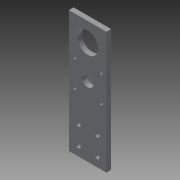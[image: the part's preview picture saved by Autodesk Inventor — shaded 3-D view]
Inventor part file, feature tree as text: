
AUTODESK INVENTOR PART (.ipt)
format: ipt  version: 2013 (Build 170138000, 138)  size: 223,744 bytes
history: native  units: in
note: dims shown in document units (in); Inventor stores cm internally (conversion verified against a paired STEP export)
features: extrude x12, sketch x12
ambient origin geometry x8: Origin, YZ Plane, XZ Plane, XY Plane, X Axis, Y Axis, Z Axis, Center Point
bodies: Solid1 (feature_tree)
feature tree (24):
  extrude  "Extrusion1"  Depth=6.688in
  extrude  "Extrusion2"  TaperAngle=90.0deg  [1 undecoded]
  extrude  "Extrusion3"  Depth=1.0in
  extrude  "Extrusion4"  Depth=2.0in
  extrude  "Extrusion5"  Depth=0.16in
  extrude  "Extrusion6"  Depth=0.16in
  extrude  "Extrusion7"  Depth=1.5in
  extrude  "Extrusion8"  TaperAngle=180.0deg  [1 undecoded]
  extrude  "Extrusion9"  TaperAngle=0.0deg  [1 undecoded]
  extrude  "Extrusion10"  Depth=0.25in
  extrude  "Extrusion11"  Depth=0.125in
  extrude  "Extrusion12"  Depth=1.75in
  sketch  "Sketch1"  dims[d0=2.0in d1=6.688in]
  sketch  "Sketch2"  dims[d2=1.0in d3=90.0deg]
  sketch  "Sketch3"  dims[d4=1.125in d5=1.0in]
  sketch  "Sketch4"  dims[d6=45.0deg d7=2.0in]
  sketch  "Sketch5"  dims[d9=0.16in d10=0.16in]
  sketch  "Sketch6"  dims[d11=0.16in d12=0.16in]
  sketch  "Sketch7"  dims[d13=2.0in d14=1.5in]
  sketch  "Sketch8"  dims[d15=0.5in d16=180.0deg]
  sketch  "Sketch9"  dims[d17=1.0in d18=0.0in]
  sketch  "Sketch10"  dims[d19=0.25in d20=0.25in]
  sketch  "Sketch11"  dims[d21=1.0in d22=0.0in d23=0.125in]
  sketch  "Sketch12"  dims[d24=0.125in d25=1.75in d26=0.75in d27=10.0in d28=0.0in d29=1.0in d30=1.0in d31=0.25in d32=0.25in d33=1.0in d34=0.0in d35=10.0in d36=0.0in d37=0.125in d38=0.0in d39=0.75in d40=0.25in d41=0.0in d43=2.938in d44=90.0deg d45=0.625in d46=1.0in d47=0.0in d48=1.125in d49=1.0in d50=0.0in d51=1.0in d52=45.0deg d53=2.0in d54=0.0in d55=0.16in d56=0.16in d57=0.16in d58=0.16in d59=0.25in d60=0.0in d61=0.25in d62=0.0in d64=2.0in d65=2.0in d66=1.0in d67=0.0in d68=1.75in d69=90.0deg d70=1.125in d71=1.0in d72=90.0deg d73=1.0in d74=90.0deg d75=0.25in d76=0.0in]
note: 3 required parameter values undecoded (feature->parameter linkage not recoverable at this tier; creation-order binding heuristic only, values carry confidence <= 0.55)
